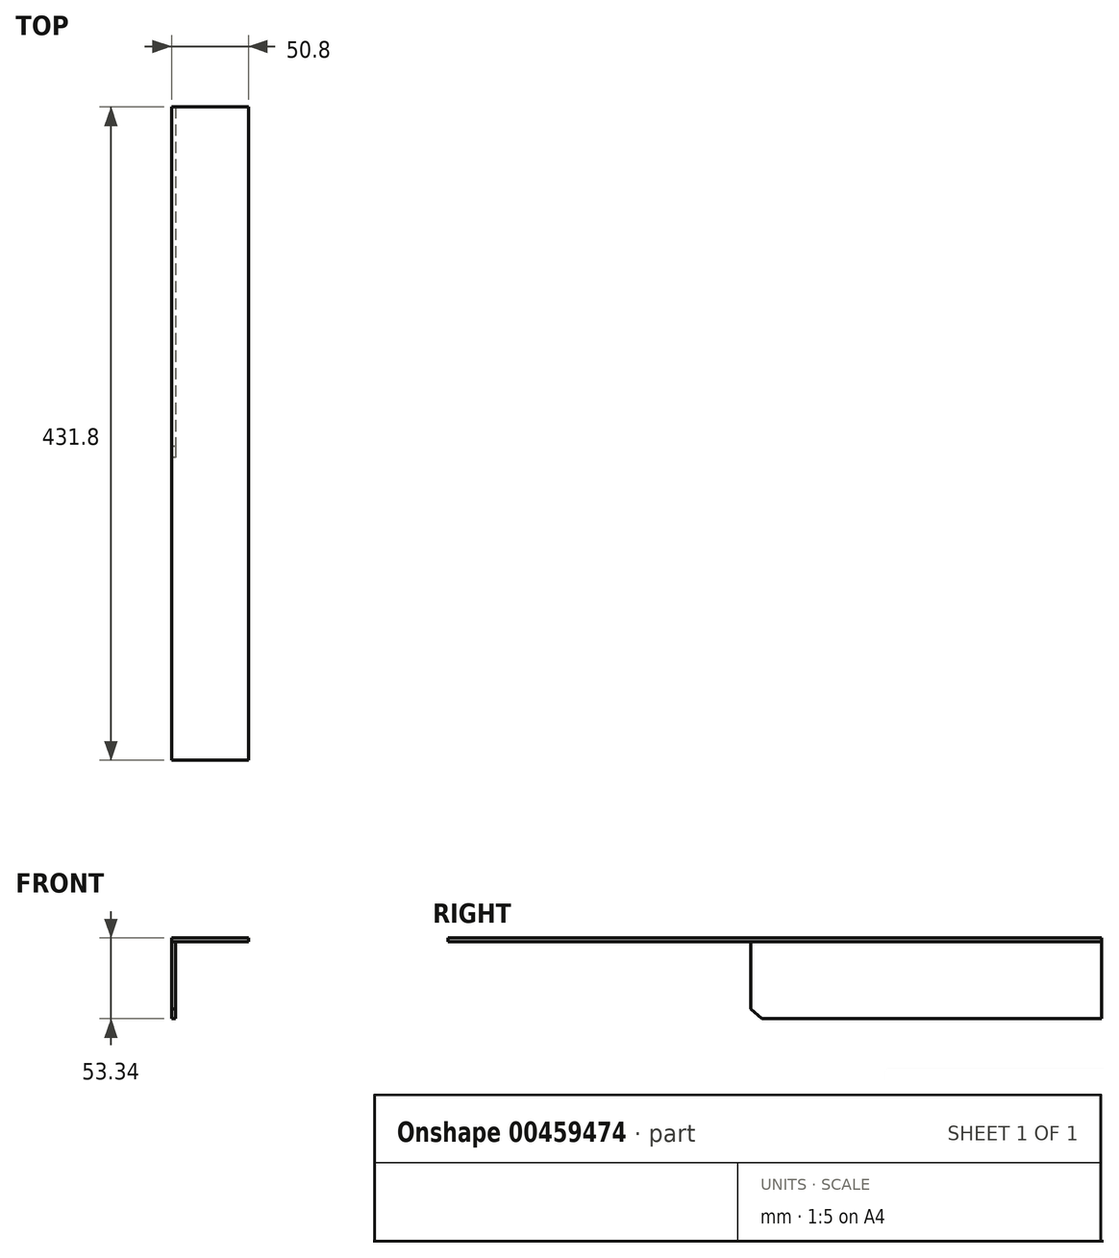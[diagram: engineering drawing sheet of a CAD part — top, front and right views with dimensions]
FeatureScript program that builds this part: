
annotation { "Feature Type Name" : "Feature", "Feature Type Description" : "" }
export const myFeature = defineFeature(function(context is Context, id is Id, definition is map)
    precondition{}
    {
        {
            var Q0;
            Q0=qCreatedBy(makeId("Top.planeOp"),FACE);
            var sketch = newSketch(context, id + "F0", { "sketchPlane" : qUnion([Q0])});
            skLineSegment(sketch, "E0", {"start": v(-56.04, 154.42) * mm, "end": v(-56.04, -277.38) * mm});
            skLineSegment(sketch, "E1", {"start": v(-56.04, -277.38) * mm, "end": v(-5.24, -277.38) * mm});
            skLineSegment(sketch, "E2", {"start": v(-5.24, -277.38) * mm, "end": v(-5.24, 154.42) * mm});
            skLineSegment(sketch, "E3", {"start": v(-5.24, 154.42) * mm, "end": v(-56.04, 154.42) * mm});
            skSolve(sketch);
        }
        {
            var Q0;
            Q0=makeQuery(id+"F0.imprint","IMPRINT",FACE,{"disambiguationData":[TD([[makeQuery(id+"F0.imprint","IMPRINT",EDGE,{"derivedFrom":sQuery(id+"F0.wireOp",EDGE,"E0")}),1.0]])]});
            extrude(context, id + "F1", {"entities" : qUnion([Q0]), "depth" : 2.54 * mm});
        }
        {
            var Q0;
            Q0=makeQuery(id+"F1.opExtrude","CAP_FACE",FACE,{"disambiguationData":[OSD([sQuery(id+"F0.wireOp",EDGE,"E0"),sQuery(id+"F0.wireOp",EDGE,"E1"),sQuery(id+"F0.wireOp",EDGE,"E2"),sQuery(id+"F0.wireOp",EDGE,"E3")])],"isStart":true});
            var sketch = newSketch(context, id + "F2", { "sketchPlane" : qUnion([Q0])});
            skLineSegment(sketch, "E4", {"start": v(-56.04, -154.42) * mm, "end": v(-53.5, -154.42) * mm});
            skLineSegment(sketch, "E5", {"start": v(-53.5, -154.42) * mm, "end": v(-53.5, 277.38) * mm});
            skLineSegment(sketch, "E6", {"start": v(-53.5, 277.38) * mm, "end": v(-56.04, 277.38) * mm});
            skLineSegment(sketch, "E7", {"start": v(-56.04, 277.38) * mm, "end": v(-56.04, -154.42) * mm});
            skSolve(sketch);
        }
        {
            var Q0;
            Q0=makeQuery(id+"F2.imprint","IMPRINT",FACE,{"disambiguationData":[TD([[makeQuery(id+"F2.imprint","IMPRINT",EDGE,{"derivedFrom":sQuery(id+"F2.wireOp",EDGE,"E4")}),-1.0]])]});
            extrude(context, id + "F3", {"entities" : qUnion([Q0]), "operationType" : NewBodyOperationType.ADD, "depth" : 50.8 * mm});
        }
        {
            var Q0;
            Q0=makeQuery(id+"F3.boolean.opBoolean","MERGE",FACE,{"derivedFrom":[makeQuery(id+"F1.opExtrude","SWEPT_FACE",FACE,{"disambiguationData":[OSD([sQuery(id+"F0.wireOp",EDGE,"E0")])]}),makeQuery(id+"F3.opExtrude","SWEPT_FACE",FACE,{"disambiguationData":[OSD([sQuery(id+"F2.wireOp",EDGE,"E7")])]})]});
            var sketch = newSketch(context, id + "F4", { "sketchPlane" : qUnion([Q0])});
            skLineSegment(sketch, "E8", {"start": v(277.38, -10.16) * mm, "end": v(143.72, -50.8) * mm});
            skSolve(sketch);
        }
        {
            var Q0;
            {var subQ0=sQuery(id+"F4.wireOp",EDGE,"E8");Q0=makeQuery(id+"F4.imprint","IMPRINT",FACE,{"disambiguationData":[TD([[makeQuery(id+"F4.imprint","IMPRINT",EDGE,{"derivedFrom":subQ0}),1.0]])]});}
            extrude(context, id + "F5", {"entities" : qUnion([Q0]), "operationType" : NewBodyOperationType.REMOVE, "oppositeDirection" : true, "depth" : 25.4 * mm});
        }
        {
            var Q0;
            Q0=makeQuery(id+"F3.boolean.opBoolean","MERGE",FACE,{"derivedFrom":[makeQuery(id+"F1.opExtrude","SWEPT_FACE",FACE,{"disambiguationData":[OSD([sQuery(id+"F0.wireOp",EDGE,"E0")])]}),makeQuery(id+"F3.opExtrude","SWEPT_FACE",FACE,{"disambiguationData":[OSD([sQuery(id+"F2.wireOp",EDGE,"E7")])]})]});
            var sketch = newSketch(context, id + "F6", { "sketchPlane" : qUnion([Q0])});
            skLineSegment(sketch, "E9", {"start": v(77.32, -50.8) * mm, "end": v(77.32, 0) * mm});
            skLineSegment(sketch, "E10", {"start": v(77.32, 0) * mm, "end": v(277.38, 0) * mm});
            skLineSegment(sketch, "E11", {"start": v(277.38, 0) * mm, "end": v(277.38, -10.16) * mm});
            skLineSegment(sketch, "E12", {"start": v(277.38, -10.16) * mm, "end": v(143.72, -50.8) * mm});
            skLineSegment(sketch, "E13", {"start": v(143.72, -50.8) * mm, "end": v(77.32, -50.8) * mm});
            skSolve(sketch);
        }
        {
            var Q0;
            Q0=makeQuery(id+"F6.imprint","IMPRINT",FACE,{"disambiguationData":[TD([[makeQuery(id+"F6.imprint","IMPRINT",EDGE,{"derivedFrom":sQuery(id+"F6.wireOp",EDGE,"E9")}),-1.0]])]});
            extrude(context, id + "F7", {"entities" : qUnion([Q0]), "operationType" : NewBodyOperationType.REMOVE, "oppositeDirection" : true, "depth" : 25.4 * mm});
        }
        {
            var Q0;
            Q0=makeQuery(id+"F3.boolean.opBoolean","MERGE",FACE,{"derivedFrom":[makeQuery(id+"F1.opExtrude","SWEPT_FACE",FACE,{"disambiguationData":[OSD([sQuery(id+"F0.wireOp",EDGE,"E0")])]}),makeQuery(id+"F3.opExtrude","SWEPT_FACE",FACE,{"disambiguationData":[OSD([sQuery(id+"F2.wireOp",EDGE,"E7")])]})]});
            var sketch = newSketch(context, id + "F8", { "sketchPlane" : qUnion([Q0])});
            skLineSegment(sketch, "E14", {"start": v(77.32, -45.65) * mm, "end": v(71.65, -50.8) * mm});
            skSolve(sketch);
        }
        {
            var Q0;
            {var subQ0=sQuery(id+"F8.wireOp",EDGE,"E14");Q0=makeQuery(id+"F8.imprint","IMPRINT",FACE,{"disambiguationData":[TD([[makeQuery(id+"F8.imprint","IMPRINT",EDGE,{"derivedFrom":subQ0}),1.0]])]});}
            extrude(context, id + "F9", {"entities" : qUnion([Q0]), "operationType" : NewBodyOperationType.REMOVE, "oppositeDirection" : true, "depth" : 25.4 * mm});
        }
        {
            var Q0;
            Q0=makeQuery(id+"F3.boolean.opBoolean","MERGE",FACE,{"derivedFrom":[makeQuery(id+"F1.opExtrude","SWEPT_FACE",FACE,{"disambiguationData":[OSD([sQuery(id+"F0.wireOp",EDGE,"E0")])]}),makeQuery(id+"F3.opExtrude","SWEPT_FACE",FACE,{"disambiguationData":[OSD([sQuery(id+"F2.wireOp",EDGE,"E7")])]})]});
            var sketch = newSketch(context, id + "F10", { "sketchPlane" : qUnion([Q0])});
            skLineSegment(sketch, "E15", {"start": v(70.1, -50.8) * mm, "end": v(77.32, -44.25) * mm});
            skSolve(sketch);
        }
        {
            var Q0;
            {var subQ0=sQuery(id+"F10.wireOp",EDGE,"E15");Q0=makeQuery(id+"F10.imprint","IMPRINT",FACE,{"disambiguationData":[TD([[makeQuery(id+"F10.imprint","IMPRINT",EDGE,{"derivedFrom":subQ0}),-1.0]])]});}
            extrude(context, id + "F11", {"entities" : qUnion([Q0]), "operationType" : NewBodyOperationType.REMOVE, "oppositeDirection" : true, "depth" : 25.4 * mm});
        }
    });
